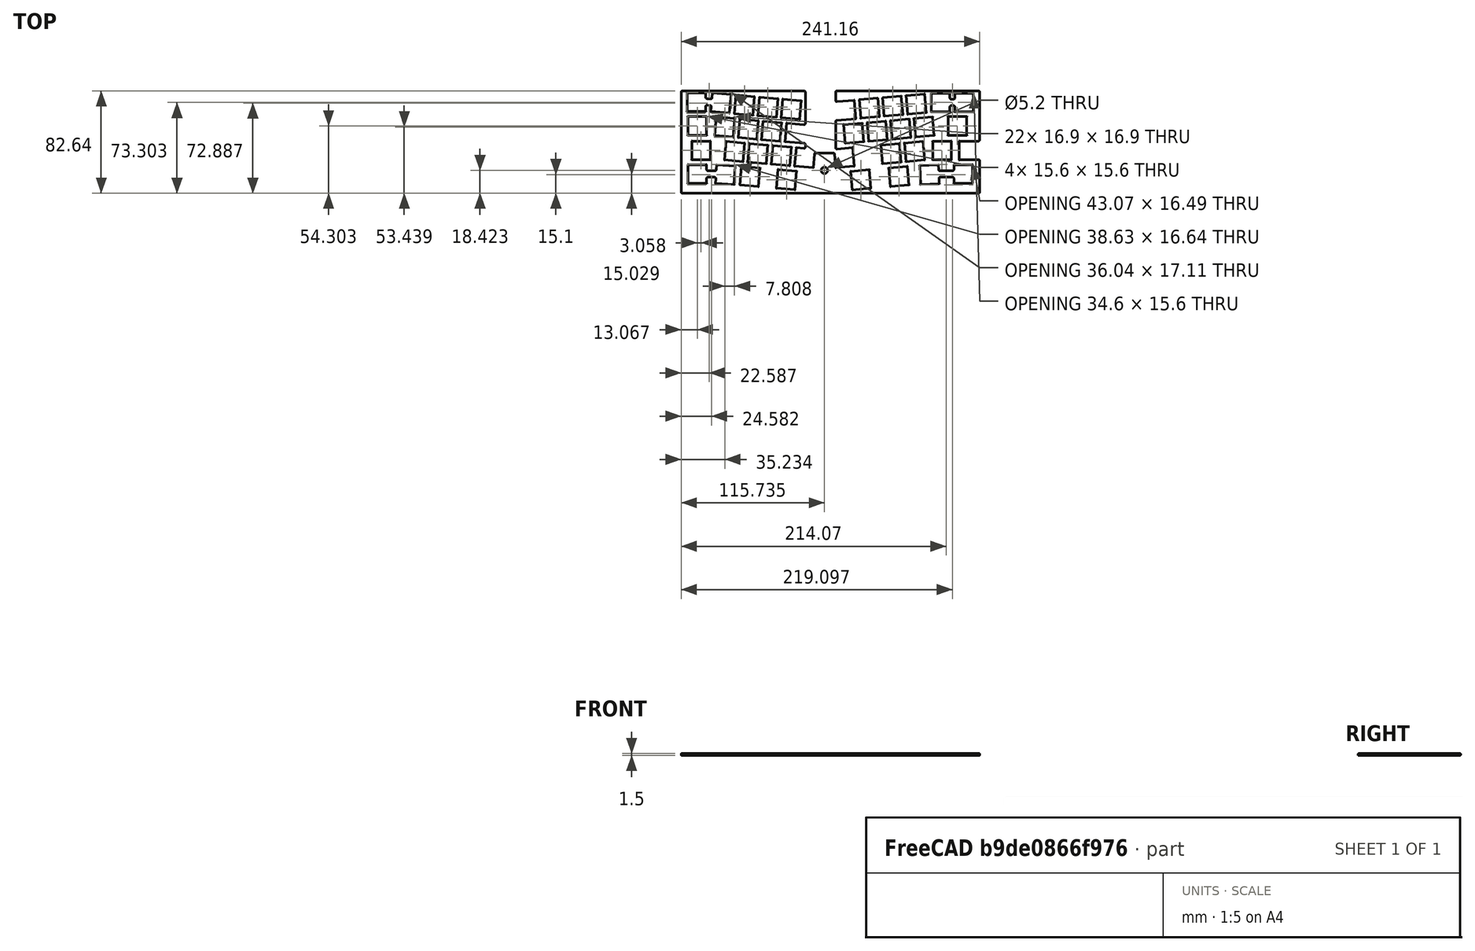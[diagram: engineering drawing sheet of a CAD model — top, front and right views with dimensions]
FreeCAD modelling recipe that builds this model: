
FCSTD DOCUMENT  (FreeCAD 0.20R)
Label: plate
License: All rights reserved
LicenseURL: http://en.wikipedia.org/wiki/All_rights_reserved
objects: Sketcher::SketchObject×1, PartDesign::Pad×1, PartDesign::Fillet×1, PartDesign::Body×1
note: 6 computed .brp shape members not serialized (recipe doc carries the construction recipe); baked Part::Feature solids carry a one-line shape summary decoded from their .brp

FEATURE [Sketcher::SketchObject] Sketch
  FullyConstrained = false
  sketch-geometry (213):
    g0: LineSegment StartX=-39.764 StartY=19.6747 StartZ=0 EndX=-38.4567 EndY=34.6176 EndZ=0
    g1: LineSegment StartX=-24.8211 StartY=18.3673 StartZ=0 EndX=-39.764 EndY=19.6747 EndZ=0
    g2: LineSegment StartX=-38.4567 StartY=34.6176 StartZ=0 EndX=-23.5138 EndY=33.3102 EndZ=0
    g3: LineSegment StartX=-23.5138 StartY=33.3102 StartZ=0 EndX=-24.8211 EndY=18.3673 EndZ=0
    g4: LineSegment StartX=-58.6917 StartY=21.3306 StartZ=0 EndX=-57.3844 EndY=36.2735 EndZ=0
    g5: LineSegment StartX=-43.7488 StartY=20.0233 StartZ=0 EndX=-58.6917 EndY=21.3306 EndZ=0
    g6: LineSegment StartX=-57.3844 StartY=36.2735 StartZ=0 EndX=-42.4415 EndY=34.9662 EndZ=0
    g7: LineSegment StartX=-42.4415 StartY=34.9662 StartZ=0 EndX=-43.7488 EndY=20.0233 EndZ=0
    g8: LineSegment StartX=-77.6194 StartY=22.9866 StartZ=0 EndX=-76.3121 EndY=37.9295 EndZ=0
    g9: LineSegment StartX=-62.6765 StartY=21.6792 StartZ=0 EndX=-77.6194 EndY=22.9866 EndZ=0
    g10: LineSegment StartX=-76.3121 StartY=37.9295 StartZ=0 EndX=-61.3692 EndY=36.6222 EndZ=0
    g11: LineSegment StartX=-61.3692 StartY=36.6222 StartZ=0 EndX=-62.6765 EndY=21.6792 EndZ=0
    g12: LineSegment StartX=-81.6042 StartY=23.3352 StartZ=0 EndX=-96.5471 EndY=24.6425 EndZ=0
    g13: LineSegment StartX=-95.2398 StartY=39.5855 StartZ=0 EndX=-80.2969 EndY=38.2781 EndZ=0
    g14: LineSegment StartX=-80.2969 StartY=38.2781 StartZ=0 EndX=-81.6042 EndY=23.3352 EndZ=0
    g15: LineSegment StartX=-93.4711 StartY=5.30084 StartZ=0 EndX=-92.1638 EndY=20.2438 EndZ=0
    g16: LineSegment StartX=-78.5282 StartY=3.9935 StartZ=0 EndX=-93.4711 EndY=5.30084 EndZ=0
    g17: LineSegment StartX=-92.1638 StartY=20.2438 StartZ=0 EndX=-77.2209 EndY=18.9364 EndZ=0
    g18: LineSegment StartX=-77.2209 StartY=18.9364 StartZ=0 EndX=-78.5282 EndY=3.9935 EndZ=0
    g19: LineSegment StartX=-74.5434 StartY=3.64488 StartZ=0 EndX=-73.2361 EndY=18.5878 EndZ=0
    g20: LineSegment StartX=-59.6005 StartY=2.33755 StartZ=0 EndX=-74.5434 EndY=3.64488 EndZ=0
    g21: LineSegment StartX=-73.2361 StartY=18.5878 StartZ=0 EndX=-58.2932 EndY=17.2805 EndZ=0
    g22: LineSegment StartX=-58.2932 StartY=17.2805 StartZ=0 EndX=-59.6005 EndY=2.33755 EndZ=0
    g23: LineSegment StartX=-55.6157 StartY=1.98892 StartZ=0 EndX=-54.3084 EndY=16.9318 EndZ=0
    g24: LineSegment StartX=-40.6728 StartY=0.681586 StartZ=0 EndX=-55.6157 EndY=1.98892 EndZ=0
    g25: LineSegment StartX=-54.3084 StartY=16.9318 StartZ=0 EndX=-39.3655 EndY=15.6245 EndZ=0
    g26: LineSegment StartX=-39.3655 StartY=15.6245 StartZ=0 EndX=-40.6728 EndY=0.681586 EndZ=0
    g27: LineSegment StartX=-36.688 StartY=0.332963 StartZ=0 EndX=-35.3807 EndY=15.2759 EndZ=0
    g28: LineSegment StartX=-85.6633 StartY=-14.4548 StartZ=0 EndX=-84.3559 EndY=0.488082 EndZ=0
    g29: LineSegment StartX=-70.7203 StartY=-15.7622 StartZ=0 EndX=-85.6633 EndY=-14.4548 EndZ=0
    g30: LineSegment StartX=-84.3559 StartY=0.488082 StartZ=0 EndX=-69.413 EndY=-0.819254 EndZ=0
    g31: LineSegment StartX=-69.413 StartY=-0.819254 StartZ=0 EndX=-70.7203 EndY=-15.7622 EndZ=0
    g32: LineSegment StartX=-66.7356 StartY=-16.1108 StartZ=0 EndX=-65.4282 EndY=-1.16788 EndZ=0
    g33: LineSegment StartX=-51.7926 StartY=-17.4181 StartZ=0 EndX=-66.7356 EndY=-16.1108 EndZ=0
    g34: LineSegment StartX=-65.4282 StartY=-1.16788 StartZ=0 EndX=-50.4853 EndY=-2.47521 EndZ=0
    g35: LineSegment StartX=-50.4853 StartY=-2.47521 StartZ=0 EndX=-51.7926 EndY=-17.4181 EndZ=0
    g36: LineSegment StartX=-47.8079 StartY=-17.7668 StartZ=0 EndX=-46.5005 EndY=-2.82384 EndZ=0
    g37: LineSegment StartX=-32.8649 StartY=-19.0741 StartZ=0 EndX=-47.8079 EndY=-17.7668 EndZ=0
    g38: LineSegment StartX=-46.5005 StartY=-2.82384 StartZ=0 EndX=-31.5576 EndY=-4.13117 EndZ=0
    g39: LineSegment StartX=-31.5576 StartY=-4.13117 StartZ=0 EndX=-32.8649 EndY=-19.0741 EndZ=0
    g40: LineSegment StartX=-28.8802 StartY=-19.4227 StartZ=0 EndX=-27.5728 EndY=-4.4798 EndZ=0
    g41: LineSegment StartX=-13.9372 StartY=-20.7301 StartZ=0 EndX=-28.8802 EndY=-19.4227 EndZ=0
    g42: LineSegment StartX=-43.6112 StartY=-37.2065 StartZ=0 EndX=-42.3038 EndY=-22.2636 EndZ=0
    g43: LineSegment StartX=-28.6683 StartY=-38.5138 StartZ=0 EndX=-43.6112 EndY=-37.2065 EndZ=0
    g44: LineSegment StartX=-42.3038 StartY=-22.2636 StartZ=0 EndX=-27.3609 EndY=-23.5709 EndZ=0
    g45: LineSegment StartX=-27.3609 StartY=-23.5709 StartZ=0 EndX=-28.6683 EndY=-38.5138 EndZ=0
    g46: LineSegment StartX=-73.1234 StartY=-34.6245 StartZ=0 EndX=-71.8161 EndY=-19.6816 EndZ=0
    g47: LineSegment StartX=-58.1805 StartY=-35.9318 StartZ=0 EndX=-73.1234 EndY=-34.6245 EndZ=0
    g48: LineSegment StartX=-71.8161 StartY=-19.6816 StartZ=0 EndX=-56.8732 EndY=-20.9889 EndZ=0
    g49: LineSegment StartX=-56.8732 StartY=-20.9889 StartZ=0 EndX=-58.1805 EndY=-35.9318 EndZ=0
    g50: LineSegment StartX=-115.714 StartY=39.8245 StartZ=0 EndX=-100.714 EndY=39.8245 EndZ=0
    g51: LineSegment StartX=-115.714 StartY=24.8245 StartZ=0 EndX=-115.714 EndY=39.8245 EndZ=0
    g52: LineSegment StartX=-100.714 StartY=24.8245 StartZ=0 EndX=-115.714 EndY=24.8245 EndZ=0
    g53: LineSegment StartX=-115.013 StartY=20.4828 StartZ=0 EndX=-100.013 EndY=20.4828 EndZ=0
    g54: LineSegment StartX=-100.013 StartY=20.4828 StartZ=0 EndX=-100.013 EndY=5.48276 EndZ=0
    g55: LineSegment StartX=-115.013 StartY=5.48276 StartZ=0 EndX=-115.013 EndY=20.4828 EndZ=0
    g56: LineSegment StartX=-100.013 StartY=5.48276 StartZ=0 EndX=-115.013 EndY=5.48276 EndZ=0
    g57: LineSegment StartX=-111.955 StartY=0.727084 StartZ=0 EndX=-96.955 EndY=0.727084 EndZ=0
    g58: LineSegment StartX=-96.955 StartY=0.727084 StartZ=0 EndX=-96.955 EndY=-14.2729 EndZ=0
    g59: LineSegment StartX=-111.955 StartY=-14.2729 StartZ=0 EndX=-111.955 EndY=0.727084 EndZ=0
    g60: LineSegment StartX=-96.955 StartY=-14.2729 StartZ=0 EndX=-111.955 EndY=-14.2729 EndZ=0
    g61: LineSegment StartX=-115.013 StartY=-18.2729 StartZ=0 EndX=-100.013 EndY=-18.2729 EndZ=0
    g62: LineSegment StartX=-115.013 StartY=-33.2729 StartZ=0 EndX=-115.013 EndY=-18.2729 EndZ=0
    g63: LineSegment StartX=-100.013 StartY=-33.2729 StartZ=0 EndX=-115.013 EndY=-33.2729 EndZ=0
    g64: LineSegment StartX=99.7278 StartY=-18.2729 StartZ=0 EndX=114.728 EndY=-18.2729 EndZ=0
    g65: LineSegment StartX=114.728 StartY=-18.2729 StartZ=0 EndX=114.728 EndY=-33.2729 EndZ=0
    g66: LineSegment StartX=114.728 StartY=-33.2729 StartZ=0 EndX=99.7278 EndY=-33.2729 EndZ=0
    g67: LineSegment StartX=104.08 StartY=-14.2729 StartZ=0 EndX=104.08 EndY=0.727084 EndZ=0
    g68: LineSegment StartX=95.0728 StartY=20.4828 StartZ=0 EndX=110.073 EndY=20.4828 EndZ=0
    g69: LineSegment StartX=110.073 StartY=20.4828 StartZ=0 EndX=110.073 EndY=5.48276 EndZ=0
    g70: LineSegment StartX=95.0728 StartY=5.48276 StartZ=0 EndX=95.0728 EndY=20.4828 EndZ=0
    g71: LineSegment StartX=110.073 StartY=5.48276 StartZ=0 EndX=95.0728 EndY=5.48276 EndZ=0
    g72: LineSegment StartX=100.517 StartY=39.4828 StartZ=0 EndX=115.517 EndY=39.4828 EndZ=0
    g73: LineSegment StartX=115.517 StartY=39.4828 StartZ=0 EndX=115.517 EndY=24.4828 EndZ=0
    g74: LineSegment StartX=115.517 StartY=24.4828 StartZ=0 EndX=100.517 EndY=24.4828 EndZ=0
    g75: LineSegment StartX=81.5174 StartY=39.4828 StartZ=0 EndX=96.5174 EndY=39.4828 EndZ=0
    g76: LineSegment StartX=81.5174 StartY=24.4828 StartZ=0 EndX=81.5174 EndY=39.4828 EndZ=0
    g77: LineSegment StartX=96.5174 StartY=24.4828 StartZ=0 EndX=81.5174 EndY=24.4828 EndZ=0
    g78: LineSegment StartX=61.143 StartY=37.4501 StartZ=0 EndX=76.0859 EndY=38.7575 EndZ=0
    g79: LineSegment StartX=76.0859 StartY=38.7575 StartZ=0 EndX=77.3933 EndY=23.8146 EndZ=0
    g80: LineSegment StartX=62.4503 StartY=22.5072 StartZ=0 EndX=61.143 EndY=37.4501 EndZ=0
    g81: LineSegment StartX=77.3933 StartY=23.8146 StartZ=0 EndX=62.4503 EndY=22.5072 EndZ=0
    g82: LineSegment StartX=42.2153 StartY=35.7942 StartZ=0 EndX=57.1582 EndY=37.1015 EndZ=0
    g83: LineSegment StartX=57.1582 StartY=37.1015 StartZ=0 EndX=58.4656 EndY=22.1586 EndZ=0
    g84: LineSegment StartX=43.5226 StartY=20.8513 StartZ=0 EndX=42.2153 EndY=35.7942 EndZ=0
    g85: LineSegment StartX=58.4656 StartY=22.1586 StartZ=0 EndX=43.5226 EndY=20.8513 EndZ=0
    g86: LineSegment StartX=67.5309 StartY=18.9364 StartZ=0 EndX=82.4738 EndY=20.2438 EndZ=0
    g87: LineSegment StartX=82.4738 StartY=20.2438 StartZ=0 EndX=83.7811 EndY=5.30084 EndZ=0
    g88: LineSegment StartX=68.8382 StartY=3.9935 StartZ=0 EndX=67.5309 EndY=18.9364 EndZ=0
    g89: LineSegment StartX=83.7811 StartY=5.30084 StartZ=0 EndX=68.8382 EndY=3.9935 EndZ=0
    g90: LineSegment StartX=59.723 StartY=-0.819254 StartZ=0 EndX=74.6659 EndY=0.488082 EndZ=0
    g91: LineSegment StartX=74.6659 StartY=0.488082 StartZ=0 EndX=75.9733 EndY=-14.4548 EndZ=0
    g92: LineSegment StartX=61.0303 StartY=-15.7622 StartZ=0 EndX=59.723 EndY=-0.819254 EndZ=0
    g93: LineSegment StartX=75.9733 StartY=-14.4548 StartZ=0 EndX=61.0303 EndY=-15.7622 EndZ=0
    g94: LineSegment StartX=40.7953 StartY=-2.47521 StartZ=0 EndX=55.7382 EndY=-1.16788 EndZ=0
    g95: LineSegment StartX=55.7382 StartY=-1.16788 StartZ=0 EndX=57.0456 EndY=-16.1108 EndZ=0
    g96: LineSegment StartX=42.1026 StartY=-17.4181 StartZ=0 EndX=40.7953 EndY=-2.47521 EndZ=0
    g97: LineSegment StartX=57.0456 StartY=-16.1108 StartZ=0 EndX=42.1026 EndY=-17.4181 EndZ=0
    g98: LineSegment StartX=48.6032 StartY=17.2805 StartZ=0 EndX=63.5461 EndY=18.5878 EndZ=0
    g99: LineSegment StartX=63.5461 StartY=18.5878 StartZ=0 EndX=64.8534 EndY=3.64488 EndZ=0
    g100: LineSegment StartX=49.9105 StartY=2.33755 StartZ=0 EndX=48.6032 EndY=17.2805 EndZ=0
    g101: LineSegment StartX=64.8534 StartY=3.64488 StartZ=0 EndX=49.9105 EndY=2.33755 EndZ=0
    g102: LineSegment StartX=29.6755 StartY=15.6245 StartZ=0 EndX=44.6184 EndY=16.9318 EndZ=0
    g103: LineSegment StartX=44.6184 StartY=16.9318 StartZ=0 EndX=45.9257 EndY=1.98892 EndZ=0
    g104: LineSegment StartX=30.9828 StartY=0.681586 StartZ=0 EndX=29.6755 EndY=15.6245 EndZ=0
    g105: LineSegment StartX=45.9257 StartY=1.98892 StartZ=0 EndX=30.9828 EndY=0.681586 EndZ=0
    g106: LineSegment StartX=23.2876 StartY=34.1382 StartZ=0 EndX=38.2305 EndY=35.4456 EndZ=0
    g107: LineSegment StartX=38.2305 StartY=35.4456 StartZ=0 EndX=39.5379 EndY=20.5026 EndZ=0
    g108: LineSegment StartX=24.5949 StartY=19.1953 StartZ=0 EndX=23.2876 EndY=34.1382 EndZ=0
    g109: LineSegment StartX=39.5379 StartY=20.5026 StartZ=0 EndX=24.5949 EndY=19.1953 EndZ=0
    g110: LineSegment StartX=19.3028 StartY=33.7896 StartZ=0 EndX=20.6102 EndY=18.8467 EndZ=0
    g111: LineSegment StartX=10.7478 StartY=13.9685 StartZ=0 EndX=25.6907 EndY=15.2759 EndZ=0
    g112: LineSegment StartX=25.6907 StartY=15.2759 StartZ=0 EndX=26.998 EndY=0.332963 EndZ=0
    g113: LineSegment StartX=12.0551 StartY=-0.974373 StartZ=0 EndX=10.7478 EndY=13.9685 EndZ=0
    g114: LineSegment StartX=26.998 StartY=0.332963 StartZ=0 EndX=12.0551 EndY=-0.974373 EndZ=0
    g115: LineSegment StartX=17.8828 StartY=-4.4798 StartZ=0 EndX=19.1902 EndY=-19.4227 EndZ=0
    g116: LineSegment StartX=19.1902 StartY=-19.4227 StartZ=0 EndX=4.24724 EndY=-20.7301 EndZ=0
    g117: LineSegment StartX=16.4257 StartY=-23.6799 StartZ=0 EndX=31.3686 EndY=-22.3725 EndZ=0
    g118: LineSegment StartX=31.3686 StartY=-22.3725 StartZ=0 EndX=32.6759 EndY=-37.3154 EndZ=0
    g119: LineSegment StartX=17.733 StartY=-38.6228 StartZ=0 EndX=16.4257 EndY=-23.6799 EndZ=0
    g120: LineSegment StartX=32.6759 StartY=-37.3154 StartZ=0 EndX=17.733 EndY=-38.6228 EndZ=0
    g121: LineSegment StartX=47.1832 StartY=-20.9889 StartZ=0 EndX=62.1261 EndY=-19.6816 EndZ=0
    g122: LineSegment StartX=62.1261 StartY=-19.6816 StartZ=0 EndX=63.4334 EndY=-34.6245 EndZ=0
    g123: LineSegment StartX=48.4905 StartY=-35.9318 StartZ=0 EndX=47.1832 EndY=-20.9889 EndZ=0
    g124: LineSegment StartX=63.4334 StartY=-34.6245 StartZ=0 EndX=48.4905 EndY=-35.9318 EndZ=0
    g125: LineSegment StartX=72.856 StartY=-34.1549 StartZ=0 EndX=72.2649 EndY=-19.1665 EndZ=0
    g126: LineSegment StartX=87.8444 StartY=-33.5637 StartZ=0 EndX=72.856 EndY=-34.1549 EndZ=0
    g127: LineSegment StartX=72.2649 StartY=-19.1665 StartZ=0 EndX=87.2532 EndY=-18.5754 EndZ=0
    g128: LineSegment StartX=-77.0007 StartY=-19.3162 StartZ=0 EndX=-77.8616 EndY=-34.2915 EndZ=0
    g129: LineSegment StartX=-77.8616 StartY=-34.2915 StartZ=0 EndX=-92.8369 EndY=-33.4306 EndZ=0
    g130: LineSegment StartX=-91.976 StartY=-18.4553 StartZ=0 EndX=-77.0007 EndY=-19.3162 EndZ=0
    g131: LineSegment StartX=104.08 StartY=0.727084 StartZ=0 EndX=119.58 EndY=0.727084 EndZ=0
    g132: ArcOfCircle CenterX=119.58 CenterY=1.72708 CenterZ=0 NormalX=0 NormalY=0 NormalZ=1 AngleXU=0 Radius=1 StartAngle=4.71239 EndAngle=6.28319
    g133: LineSegment StartX=119.58 StartY=-14.2729 StartZ=0 EndX=104.08 EndY=-14.2729 EndZ=0
    g134: ArcOfCircle CenterX=119.58 CenterY=-15.2729 CenterZ=0 NormalX=0 NormalY=0 NormalZ=1 AngleXU=0 Radius=1 StartAngle=0 EndAngle=1.5708
    g135: LineSegment StartX=120.58 StartY=-15.2729 StartZ=0 EndX=120.58 EndY=-40.3245 EndZ=0
    g136: ArcOfCircle CenterX=119.58 CenterY=-40.3245 CenterZ=0 NormalX=0 NormalY=0 NormalZ=1 AngleXU=0 Radius=1 StartAngle=4.71239 EndAngle=6.28319
    g137: LineSegment StartX=82.61 StartY=0.727084 StartZ=0 EndX=97.61 EndY=0.727084 EndZ=0
    g138: LineSegment StartX=97.61 StartY=0.727084 StartZ=0 EndX=97.61 EndY=-14.2729 EndZ=0
    g139: LineSegment StartX=82.61 StartY=-14.2729 StartZ=0 EndX=82.61 EndY=0.727084 EndZ=0
    g140: LineSegment StartX=97.61 StartY=-14.2729 StartZ=0 EndX=82.61 EndY=-14.2729 EndZ=0
    g141: LineSegment StartX=99.7278 StartY=-33.2729 StartZ=0 EndX=99.7278 EndY=-29.3882 EndZ=0
    g142: ArcOfCircle CenterX=98.7278 CenterY=-29.3882 CenterZ=0 NormalX=0 NormalY=0 NormalZ=1 AngleXU=0 Radius=1 StartAngle=0 EndAngle=1.5708
    g143: LineSegment StartX=99.7278 StartY=-22.1882 StartZ=0 EndX=99.7278 EndY=-18.2729 EndZ=0
    g144: ArcOfCircle CenterX=98.7278 CenterY=-22.1882 CenterZ=0 NormalX=0 NormalY=0 NormalZ=1 AngleXU=0 Radius=1 StartAngle=4.71239 EndAngle=6.28319
    g145: LineSegment StartX=88.3965 StartY=-23.1882 StartZ=0 EndX=98.7278 EndY=-23.1882 EndZ=0
    g146: LineSegment StartX=87.2532 StartY=-18.5754 StartZ=0 EndX=87.3973 EndY=-22.2276 EndZ=0
    g147: ArcOfCircle CenterX=88.3965 CenterY=-22.1882 CenterZ=0 NormalX=0 NormalY=0 NormalZ=1 AngleXU=0 Radius=1 StartAngle=3.18101 EndAngle=4.71239
    g148: LineSegment StartX=88.6805 StartY=-28.3882 StartZ=0 EndX=98.7278 EndY=-28.3882 EndZ=0
    g149: LineSegment StartX=87.6812 StartY=-29.4276 StartZ=0 EndX=87.8444 EndY=-33.5637 EndZ=0
    g150: ArcOfCircle CenterX=88.6805 CenterY=-29.3882 CenterZ=0 NormalX=0 NormalY=0 NormalZ=1 AngleXU=0 Radius=1 StartAngle=1.5708 EndAngle=3.18101
    g151: LineSegment StartX=120.58 StartY=40.3245 StartZ=0 EndX=120.58 EndY=1.72708 EndZ=0
    g152: ArcOfCircle CenterX=119.58 CenterY=40.3245 CenterZ=0 NormalX=0 NormalY=0 NormalZ=1 AngleXU=0 Radius=1 StartAngle=0 EndAngle=1.5708
    g153: LineSegment StartX=-27.5728 StartY=-4.4798 StartZ=0 EndX=-21.3582 EndY=-5.0235 EndZ=0
    g154: ArcOfCircle CenterX=-21.2711 CenterY=-4.02731 CenterZ=0 NormalX=0 NormalY=0 NormalZ=1 AngleXU=0 Radius=1 StartAngle=4.62512 EndAngle=6.28319
    g155: LineSegment StartX=-21.1839 StartY=-1.02347 StartZ=0 EndX=-36.688 EndY=0.332963 EndZ=0
    g156: LineSegment StartX=-20.2711 StartY=-4.02731 StartZ=0 EndX=-20.2711 EndY=-2.01967 EndZ=0
    g157: ArcOfCircle CenterX=-21.2711 CenterY=-2.01967 CenterZ=0 NormalX=0 NormalY=0 NormalZ=1 AngleXU=0 Radius=1 StartAngle=0 EndAngle=1.48353
    g158: LineSegment StartX=5.28036 StartY=-5.58237 StartZ=0 EndX=17.8828 EndY=-4.4798 EndZ=0
    g159: ArcOfCircle CenterX=5.19321 CenterY=-4.58617 CenterZ=0 NormalX=0 NormalY=0 NormalZ=1 AngleXU=0 Radius=1 StartAngle=3.14159 EndAngle=4.79966
    g160: LineSegment StartX=-12.9722 StartY=-9.69998 StartZ=0 EndX=-13.9372 EndY=-20.7301 EndZ=0
    g161: ArcOfCircle CenterX=-11.976 CenterY=-9.78713 CenterZ=0 NormalX=0 NormalY=0 NormalZ=1 AngleXU=0 Radius=1 StartAngle=1.5708 EndAngle=3.05433
    g162: LineSegment StartX=-35.3807 StartY=15.2759 StartZ=0 EndX=-21.3582 EndY=14.0491 EndZ=0
    g163: ArcOfCircle CenterX=-21.2711 CenterY=15.0453 CenterZ=0 NormalX=0 NormalY=0 NormalZ=1 AngleXU=0 Radius=1 StartAngle=4.62512 EndAngle=6.28319
    g164: LineSegment StartX=-20.2711 StartY=15.0453 StartZ=0 EndX=-20.2711 EndY=40.3245 EndZ=0
    g165: ArcOfCircle CenterX=-21.2711 CenterY=40.3245 CenterZ=0 NormalX=0 NormalY=0 NormalZ=1 AngleXU=0 Radius=1 StartAngle=0 EndAngle=1.5708
    g166: ArcOfCircle CenterX=5.19321 CenterY=40.3245 CenterZ=0 NormalX=0 NormalY=0 NormalZ=1 AngleXU=0 Radius=1 StartAngle=1.5708 EndAngle=3.14159
    g167: LineSegment StartX=5.28036 StartY=32.5628 StartZ=0 EndX=19.3028 EndY=33.7896 EndZ=0
    g168: LineSegment StartX=4.19321 StartY=40.3245 StartZ=0 EndX=4.19321 EndY=33.559 EndZ=0
    g169: ArcOfCircle CenterX=5.19321 CenterY=33.559 CenterZ=0 NormalX=0 NormalY=0 NormalZ=1 AngleXU=0 Radius=1 StartAngle=3.14159 EndAngle=4.79966
    g170: LineSegment StartX=20.6102 StartY=18.8467 StartZ=0 EndX=5.10605 EndY=17.4902 EndZ=0
    g171: LineSegment StartX=4.19321 StartY=16.494 StartZ=0 EndX=4.19321 EndY=-4.58617 EndZ=0
    g172: ArcOfCircle CenterX=5.19321 CenterY=16.494 CenterZ=0 NormalX=0 NormalY=0 NormalZ=1 AngleXU=0 Radius=1 StartAngle=1.65806 EndAngle=3.14159
    g173: LineSegment StartX=-100.714 StartY=28.8263 StartZ=0 EndX=-100.714 EndY=24.8245 EndZ=0
    g174: ArcOfCircle CenterX=-99.7138 CenterY=28.8263 CenterZ=0 NormalX=0 NormalY=0 NormalZ=1 AngleXU=0 Radius=1 StartAngle=1.48353 EndAngle=3.14159
    g175: LineSegment StartX=-97.117 StartY=29.6029 StartZ=0 EndX=-99.6267 EndY=29.8225 EndZ=0
    g176: LineSegment StartX=-96.5471 StartY=24.6425 StartZ=0 EndX=-96.2079 EndY=28.5195 EndZ=0
    g177: ArcOfCircle CenterX=-97.2041 CenterY=28.6067 CenterZ=0 NormalX=0 NormalY=0 NormalZ=1 AngleXU=0 Radius=1 StartAngle=6.19592 EndAngle=7.76672
    g178: LineSegment StartX=-95.5821 StartY=35.6724 StartZ=0 EndX=-95.2398 EndY=39.5855 EndZ=0
    g179: ArcOfCircle CenterX=-96.5783 CenterY=35.7596 CenterZ=0 NormalX=0 NormalY=0 NormalZ=1 AngleXU=0 Radius=1 StartAngle=4.62512 EndAngle=6.19592
    g180: LineSegment StartX=-96.6655 StartY=34.7634 StartZ=0 EndX=-99.801 EndY=35.0377 EndZ=0
    g181: LineSegment StartX=-100.714 StartY=39.8245 StartZ=0 EndX=-100.714 EndY=36.0339 EndZ=0
    g182: ArcOfCircle CenterX=-99.7138 CenterY=36.0339 CenterZ=0 NormalX=0 NormalY=0 NormalZ=1 AngleXU=0 Radius=1 StartAngle=3.14159 EndAngle=4.62512
    g183: LineSegment StartX=-92.8369 StartY=-33.4306 StartZ=0 EndX=-92.6085 EndY=-29.458 EndZ=0
    g184: ArcOfCircle CenterX=-93.6068 CenterY=-29.4006 CenterZ=0 NormalX=0 NormalY=0 NormalZ=1 AngleXU=0 Radius=1 StartAngle=6.22576 EndAngle=7.85398
    g185: LineSegment StartX=-99.0128 StartY=-28.4006 StartZ=0 EndX=-93.6068 EndY=-28.4006 EndZ=0
    g186: LineSegment StartX=-100.013 StartY=-29.4006 StartZ=0 EndX=-100.013 EndY=-33.2729 EndZ=0
    g187: ArcOfCircle CenterX=-99.0128 CenterY=-29.4006 CenterZ=0 NormalX=0 NormalY=0 NormalZ=1 AngleXU=0 Radius=1 StartAngle=1.5708 EndAngle=3.14159
    g188: LineSegment StartX=-100.013 StartY=-18.2729 StartZ=0 EndX=-100.013 EndY=-22.2006 EndZ=0
    g189: ArcOfCircle CenterX=-99.0128 CenterY=-22.2006 CenterZ=0 NormalX=0 NormalY=0 NormalZ=1 AngleXU=0 Radius=1 StartAngle=3.14159 EndAngle=4.71239
    g190: LineSegment StartX=-99.0128 StartY=-23.2006 StartZ=0 EndX=-93.193 EndY=-23.2006 EndZ=0
    g191: LineSegment StartX=-92.1946 StartY=-22.258 StartZ=0 EndX=-91.976 EndY=-18.4553 EndZ=0
    g192: ArcOfCircle CenterX=-93.193 CenterY=-22.2006 CenterZ=0 NormalX=0 NormalY=0 NormalZ=1 AngleXU=0 Radius=1 StartAngle=4.71239 EndAngle=6.22576
    g193: Circle CenterX=-4.845 CenterY=-22.8968 CenterZ=0 NormalX=0 NormalY=0 NormalZ=-1 AngleXU=0 Radius=2.6
    g194: LineSegment StartX=-119.58 StartY=41.3245 StartZ=0 EndX=-21.2711 EndY=41.3245 EndZ=0
    g195: ArcOfCircle CenterX=-119.58 CenterY=40.3245 CenterZ=0 NormalX=0 NormalY=0 NormalZ=1 AngleXU=0 Radius=1 StartAngle=1.5708 EndAngle=3.14159
    g196: LineSegment StartX=119.58 StartY=-41.3245 StartZ=0 EndX=-119.58 EndY=-41.3245 EndZ=0
    g197: LineSegment StartX=-120.58 StartY=-40.3245 StartZ=0 EndX=-120.58 EndY=40.3245 EndZ=0
    g198: ArcOfCircle CenterX=-119.58 CenterY=-40.3245 CenterZ=0 NormalX=0 NormalY=0 NormalZ=1 AngleXU=0 Radius=1 StartAngle=3.14159 EndAngle=4.71239
    g199: LineSegment StartX=2.28604 StartY=-8.78713 StartZ=0 EndX=-11.976 EndY=-8.78713 EndZ=0
    g200: LineSegment StartX=4.24724 StartY=-20.7301 StartZ=0 EndX=3.28223 EndY=-9.69998 EndZ=0
    g201: ArcOfCircle CenterX=2.28604 CenterY=-9.78713 CenterZ=0 NormalX=0 NormalY=0 NormalZ=1 AngleXU=0 Radius=1 StartAngle=0.0872665 EndAngle=1.5708
    g202: LineSegment StartX=119.58 StartY=41.3245 StartZ=0 EndX=5.19321 EndY=41.3245 EndZ=0
    g203: LineSegment StartX=96.5174 StartY=39.4828 StartZ=0 EndX=96.5174 EndY=35.5828 EndZ=0
    g204: ArcOfCircle CenterX=97.5174 CenterY=35.5828 CenterZ=0 NormalX=0 NormalY=0 NormalZ=1 AngleXU=0 Radius=1 StartAngle=3.14159 EndAngle=4.71239
    g205: LineSegment StartX=100.517 StartY=35.5828 StartZ=0 EndX=100.517 EndY=39.4828 EndZ=0
    g206: LineSegment StartX=97.5174 StartY=34.5828 StartZ=0 EndX=99.5174 EndY=34.5828 EndZ=0
    g207: ArcOfCircle CenterX=99.5174 CenterY=35.5828 CenterZ=0 NormalX=0 NormalY=0 NormalZ=1 AngleXU=0 Radius=1 StartAngle=4.71239 EndAngle=6.28319
    g208: LineSegment StartX=96.5174 StartY=28.3828 StartZ=0 EndX=96.5174 EndY=24.4828 EndZ=0
    g209: ArcOfCircle CenterX=97.5174 CenterY=28.3828 CenterZ=0 NormalX=0 NormalY=0 NormalZ=1 AngleXU=0 Radius=1 StartAngle=1.5708 EndAngle=3.14159
    g210: LineSegment StartX=97.5174 StartY=29.3828 StartZ=0 EndX=99.5174 EndY=29.3828 EndZ=0
    g211: LineSegment StartX=100.517 StartY=24.4828 StartZ=0 EndX=100.517 EndY=28.3828 EndZ=0
    g212: ArcOfCircle CenterX=99.5174 CenterY=28.3828 CenterZ=0 NormalX=0 NormalY=0 NormalZ=1 AngleXU=0 Radius=1 StartAngle=0 EndAngle=1.5708
  constraints (212):
    c: Coincident(g197,g198)
    c: Coincident(g195,g197)
    c: Coincident(g196,g198)
    c: Coincident(g194,g195)
    c: Coincident(g51,g52)
    c: Coincident(g50,g51)
    c: Coincident(g62,g63)
    c: Coincident(g61,g62)
    c: Coincident(g55,g56)
    c: Coincident(g53,g55)
    c: Coincident(g59,g60)
    c: Coincident(g57,g59)
    c: Coincident(g52,g173)
    c: Coincident(g173,g174)
    c: Coincident(g181,g182)
    c: Coincident(g50,g181)
    c: Coincident(g63,g186)
    c: Coincident(g186,g187)
    c: Coincident(g188,g189)
    c: Coincident(g61,g188)
    c: Coincident(g54,g56)
    c: Coincident(g53,g54)
    c: Coincident(g180,g182)
    c: Coincident(g174,g175)
    c: Coincident(g185,g187)
    c: Coincident(g189,g190)
    c: Coincident(g175,g177)
    c: Coincident(g58,g60)
    c: Coincident(g57,g58)
    c: Coincident(g179,g180)
    c: Coincident(g12,g176)
    c: Coincident(g176,g177)
    c: Coincident(g178,g179)
    c: Coincident(g13,g178)
    c: Coincident(g184,g185)
    c: Coincident(g15,g16)
    c: Coincident(g190,g192)
    c: Coincident(g129,g183)
    c: Coincident(g183,g184)
    c: Coincident(g191,g192)
    c: Coincident(g15,g17)
    c: Coincident(g130,g191)
    c: Coincident(g28,g29)
    c: Coincident(g28,g30)
    c: Coincident(g12,g14)
    c: Coincident(g13,g14)
    c: Coincident(g16,g18)
    c: Coincident(g128,g129)
    c: Coincident(g8,g9)
    c: Coincident(g17,g18)
    c: Coincident(g128,g130)
    c: Coincident(g8,g10)
    c: Coincident(g19,g20)
    c: Coincident(g19,g21)
    c: Coincident(g46,g47)
    c: Coincident(g46,g48)
    c: Coincident(g29,g31)
    c: Coincident(g30,g31)
    c: Coincident(g32,g33)
    c: Coincident(g32,g34)
    c: Coincident(g9,g11)
    c: Coincident(g10,g11)
    c: Coincident(g20,g22)
    c: Coincident(g4,g5)
    c: Coincident(g21,g22)
    c: Coincident(g47,g49)
    c: Coincident(g4,g6)
    c: Coincident(g48,g49)
    c: Coincident(g23,g24)
    c: Coincident(g23,g25)
    c: Coincident(g33,g35)
    c: Coincident(g34,g35)
    c: Coincident(g36,g37)
    c: Coincident(g36,g38)
    c: Coincident(g5,g7)
    c: Coincident(g42,g43)
    c: Coincident(g6,g7)
    c: Coincident(g42,g44)
    c: Coincident(g24,g26)
    c: Coincident(g0,g1)
    c: Coincident(g25,g26)
    c: Coincident(g0,g2)
    c: Coincident(g27,g155)
    c: Coincident(g27,g162)
    c: Coincident(g37,g39)
    c: Coincident(g38,g39)
    c: Coincident(g40,g41)
    c: Coincident(g43,g45)
    c: Coincident(g40,g153)
    c: Coincident(g44,g45)
    c: Coincident(g1,g3)
    c: Coincident(g2,g3)
    c: Coincident(g153,g154)
    c: Coincident(g162,g163)
    c: Coincident(g165,g194)
    c: Coincident(g155,g157)
    c: Coincident(g154,g156)
    c: Coincident(g156,g157)
    c: Coincident(g163,g164)
    c: Coincident(g164,g165)
    c: Coincident(g41,g160)
    c: Coincident(g160,g161)
    c: Coincident(g161,g199)
    c: Coincident(g199,g201)
    c: Coincident(g200,g201)
    c: Coincident(g159,g171)
    c: Coincident(g171,g172)
    c: Coincident(g168,g169)
    c: Coincident(g166,g168)
    c: Coincident(g116,g200)
    c: Coincident(g170,g172)
    c: Coincident(g166,g202)
    c: Coincident(g158,g159)
    c: Coincident(g167,g169)
    c: Coincident(g111,g113)
    c: Coincident(g113,g114)
    c: Coincident(g117,g119)
    c: Coincident(g119,g120)
    c: Coincident(g115,g158)
    c: Coincident(g115,g116)
    c: Coincident(g110,g167)
    c: Coincident(g110,g170)
    c: Coincident(g106,g108)
    c: Coincident(g108,g109)
    c: Coincident(g111,g112)
    c: Coincident(g112,g114)
    c: Coincident(g102,g104)
    c: Coincident(g104,g105)
    c: Coincident(g117,g118)
    c: Coincident(g118,g120)
    c: Coincident(g106,g107)
    c: Coincident(g107,g109)
    c: Coincident(g94,g96)
    c: Coincident(g96,g97)
    c: Coincident(g82,g84)
    c: Coincident(g84,g85)
    c: Coincident(g102,g103)
    c: Coincident(g103,g105)
    c: Coincident(g121,g123)
    c: Coincident(g123,g124)
    c: Coincident(g98,g100)
    c: Coincident(g100,g101)
    c: Coincident(g94,g95)
    c: Coincident(g95,g97)
    c: Coincident(g82,g83)
    c: Coincident(g83,g85)
    c: Coincident(g90,g92)
    c: Coincident(g92,g93)
    c: Coincident(g78,g80)
    c: Coincident(g121,g122)
    c: Coincident(g80,g81)
    c: Coincident(g122,g124)
    c: Coincident(g98,g99)
    c: Coincident(g99,g101)
    c: Coincident(g86,g88)
    c: Coincident(g88,g89)
    c: Coincident(g125,g127)
    c: Coincident(g125,g126)
    c: Coincident(g90,g91)
    c: Coincident(g91,g93)
    c: Coincident(g78,g79)
    c: Coincident(g79,g81)
    c: Coincident(g76,g77)
    c: Coincident(g75,g76)
    c: Coincident(g86,g87)
    c: Coincident(g139,g140)
    c: Coincident(g137,g139)
    c: Coincident(g87,g89)
    c: Coincident(g127,g146)
    c: Coincident(g146,g147)
    c: Coincident(g149,g150)
    c: Coincident(g126,g149)
    c: Coincident(g145,g147)
    c: Coincident(g148,g150)
    c: Coincident(g70,g71)
    c: Coincident(g68,g70)
    c: Coincident(g77,g208)
    c: Coincident(g208,g209)
    c: Coincident(g203,g204)
    c: Coincident(g75,g203)
    c: Coincident(g209,g210)
    c: Coincident(g204,g206)
    c: Coincident(g138,g140)
    c: Coincident(g137,g138)
    c: Coincident(g142,g148)
    c: Coincident(g144,g145)
    c: Coincident(g210,g212)
    c: Coincident(g206,g207)
    c: Coincident(g66,g141)
    c: Coincident(g141,g142)
    c: Coincident(g143,g144)
    c: Coincident(g64,g143)
    c: Coincident(g74,g211)
    c: Coincident(g211,g212)
    c: Coincident(g205,g207)
    c: Coincident(g72,g205)
    c: Coincident(g67,g133)
    c: Coincident(g67,g131)
    c: Coincident(g69,g71)
    c: Coincident(g68,g69)
    c: Coincident(g65,g66)
    c: Coincident(g64,g65)
    c: Coincident(g73,g74)
    c: Coincident(g72,g73)
    c: Coincident(g136,g196)
    c: Coincident(g133,g134)
    c: Coincident(g131,g132)
    c: Coincident(g152,g202)
    c: Coincident(g135,g136)
    c: Coincident(g134,g135)
    c: Coincident(g132,g151)
    c: Coincident(g151,g152)
FEATURE [PartDesign::Pad] Pad
  Direction = (0,0,1)
  Length = 1.5
  Length2 = 10
  Profile = -> Sketch
  ReferenceAxis = -> Sketch [N_Axis]
  Type = 0
FEATURE [PartDesign::Fillet] Fillet
  Base = -> Pad [Face215,Face214]
  BaseFeature = -> Pad
  Radius = 0.3
  SupportTransform = false
  UseAllEdges = false
FEATURE [PartDesign::Body] Body
  Group = -> [Sketch,Pad,Fillet]
  Origin = -> Origin
  Tip = -> Fillet
